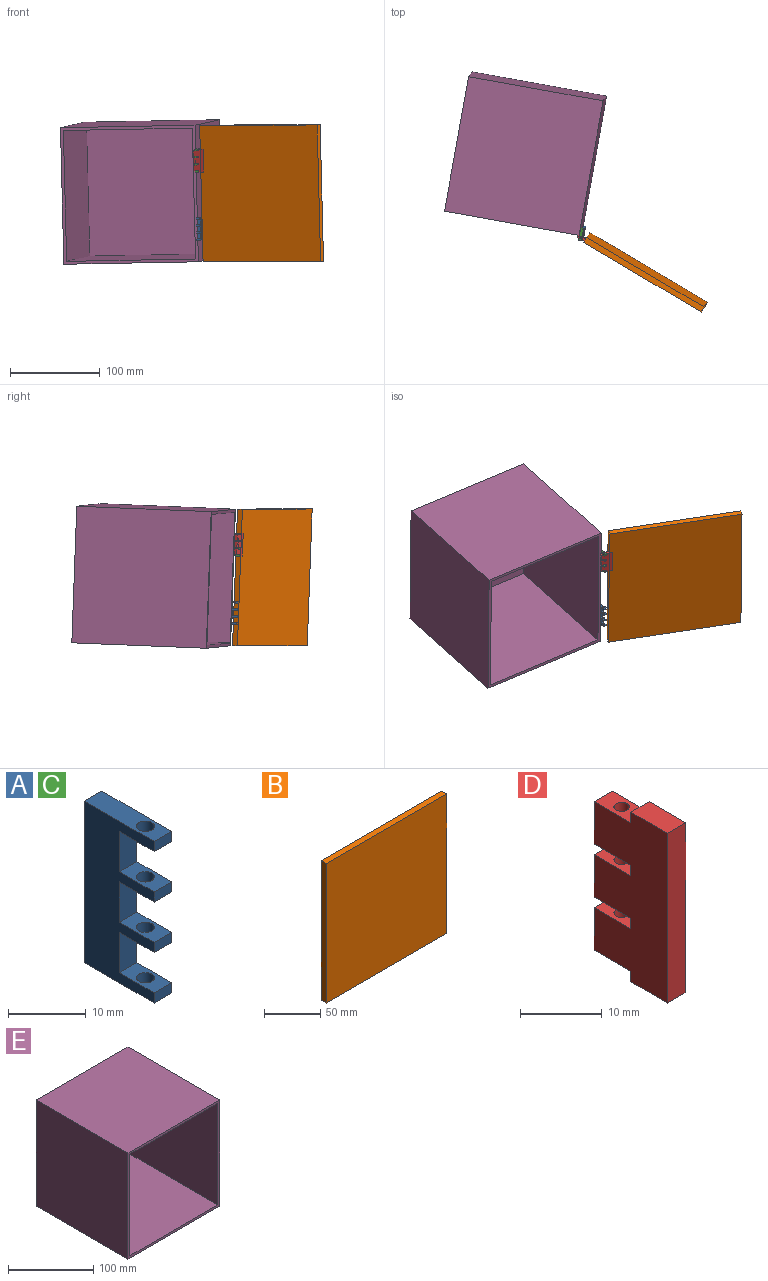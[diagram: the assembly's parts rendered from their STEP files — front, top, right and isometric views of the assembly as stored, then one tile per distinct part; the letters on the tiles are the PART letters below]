
ASSEMBLY  parts=5 mates=8
PART A: 22 faces, bbox 3.2x12.7x25.4 mm
  f0: plane 12.7x3.18mm, normal (0,0,1), area 36.1mm2, adj f1,f15,f16,f17,f21
  f1: plane 3.18x1.59mm, normal (0,-1,0), area 5mm2, adj f0,f2,f16,f17
  f2: plane 6.35x3.18mm, normal (0,0,-1), area 16mm2, adj f1,f3,f16,f17,f21
  f3: plane 6.35x3.18mm, normal (0,-1,0), area 20.2mm2, adj f2,f4,f16,f17
  f4: plane 6.35x3.18mm, normal (0,0,1), area 16mm2, adj f3,f5,f16,f17,f20
  f5: plane 3.18x1.59mm, normal (0,-1,0), area 5mm2, adj f4,f6,f16,f17
  f6: plane 6.35x3.18mm, normal (0,0,-1), area 16mm2, adj f5,f7,f16,f17,f20
  f7: plane 6.35x3.18mm, normal (0,-1,0), area 20.2mm2, adj f6,f8,f16,f17
  f8: plane 6.35x3.18mm, normal (0,0,1), area 16mm2, adj f7,f9,f16,f17,f19
  f9: plane 3.18x1.59mm, normal (0,-1,0), area 5mm2, adj f8,f10,f16,f17
  f10: plane 6.35x3.18mm, normal (0,0,-1), area 16mm2, adj f9,f11,f16,f17,f19
  f11: plane 6.35x3.18mm, normal (0,-1,0), area 20.2mm2, adj f10,f12,f16,f17
  f12: plane 6.35x3.18mm, normal (0,0,1), area 16mm2, adj f11,f13,f16,f17,f18
  f13: plane 3.18x1.59mm, normal (0,-1,0), area 5mm2, adj f12,f14,f16,f17
  f14: plane 12.7x3.18mm, normal (0,0,-1), area 36.1mm2, adj f13,f15,f16,f17,f18
  f15: plane 25.4x3.18mm, normal (0,1,0), area 80.6mm2, adj f0,f14,f16,f17
  f16: plane 25.4x12.7mm, normal (1,0,0), area 201.6mm2, adj f0,f1,f2,f3,f4,f5,f6,f7
  f17: plane 25.4x12.7mm, normal (-1,0,0), area 201.6mm2, adj f0,f1,f2,f3,f4,f5,f6,f7
  f18: cylinder r=1.15mm len=2.31mm, axis (0,0,1), area 11.5mm2, adj f12,f14
  f19: cylinder r=1.15mm len=2.31mm, axis (0,0,1), area 11.5mm2, adj f8,f10
  f20: cylinder r=1.15mm len=2.31mm, axis (0,0,1), area 11.5mm2, adj f4,f6
  f21: cylinder r=1.15mm len=2.31mm, axis (0,0,1), area 11.5mm2, adj f0,f2
PART B: 6 faces, bbox 152.4x6.4x152.4 mm
  f0: plane 152.4x6.35mm, normal (0,0,1), area 967.7mm2, adj f1,f3,f4,f5
  f1: plane 152.4x6.35mm, normal (-1,0,0), area 967.7mm2, adj f0,f2,f4,f5
  f2: plane 152.4x6.35mm, normal (0,0,-1), area 967.7mm2, adj f1,f3,f4,f5
  f3: plane 152.4x6.35mm, normal (1,0,0), area 967.7mm2, adj f0,f2,f4,f5
  f4: plane 152.4x152.4mm, normal (0,-1,0), area 23225.8mm2, adj f0,f1,f2,f3
  f5: plane 152.4x152.4mm, normal (0,1,0), area 23225.8mm2, adj f0,f1,f2,f3
PART C: same geometry as A
PART D: 21 faces, bbox 3.2x12.7x25.4 mm
  f0: plane 3.18x1.59mm, normal (0,1,0), area 5mm2, adj f1,f15,f16,f17
  f1: plane 6.35x3.18mm, normal (0,0,-1), area 17.4mm2, adj f0,f2,f16,f17,f20
  f2: plane 6.35x3.18mm, normal (0,1,0), area 20.2mm2, adj f1,f3,f16,f17
  f3: plane 6.35x3.18mm, normal (0,0,1), area 17.4mm2, adj f2,f4,f16,f17,f20
  f4: plane 3.18x1.59mm, normal (0,1,0), area 5mm2, adj f3,f5,f16,f17
  f5: plane 6.35x3.18mm, normal (0,0,1), area 20.2mm2, adj f4,f6,f16,f17
  f6: plane 25.4x3.18mm, normal (0,-1,0), area 80.6mm2, adj f5,f7,f16,f17
  f7: plane 6.35x3.18mm, normal (0,0,-1), area 20.2mm2, adj f6,f8,f16,f17
  f8: plane 3.18x1.59mm, normal (0,1,0), area 5mm2, adj f7,f9,f16,f17
  f9: plane 6.35x3.18mm, normal (0,0,-1), area 17.4mm2, adj f8,f10,f16,f17,f19
  f10: plane 6.35x3.18mm, normal (0,1,0), area 20.2mm2, adj f9,f11,f16,f17
  f11: plane 6.35x3.18mm, normal (0,0,1), area 17.4mm2, adj f10,f12,f16,f17,f19
  f12: plane 3.18x1.59mm, normal (0,1,0), area 5mm2, adj f11,f13,f16,f17
  f13: plane 6.35x3.18mm, normal (0,0,-1), area 17.4mm2, adj f12,f14,f16,f17,f18
  f14: plane 6.35x3.18mm, normal (0,1,0), area 20.2mm2, adj f13,f15,f16,f17
  f15: plane 6.35x3.18mm, normal (0,0,1), area 17.4mm2, adj f0,f14,f16,f17,f18
  f16: plane 25.4x12.7mm, normal (1,0,0), area 282.3mm2, adj f0,f1,f2,f3,f4,f5,f6,f7
  f17: plane 25.4x12.7mm, normal (-1,0,0), area 282.3mm2, adj f0,f1,f2,f3,f4,f5,f6,f7
  f18: cylinder r=0.94mm len=6.35mm, axis (0,0,1), area 37.4mm2, adj f13,f15
  f19: cylinder r=0.94mm len=6.35mm, axis (0,0,1), area 37.4mm2, adj f9,f11
  f20: cylinder r=0.94mm len=6.35mm, axis (0,0,1), area 37.4mm2, adj f1,f3
PART E: 11 faces, bbox 152.4x152.4x152.4 mm
  f0: plane 152.4x152.4mm, normal (0,-1,0), area 1895.2mm2, adj f1,f3,f4,f5,f6,f7,f8,f9
  f1: plane 152.4x152.4mm, normal (1,0,0), area 23225.8mm2, adj f0,f2,f4,f5
  f2: plane 152.4x152.4mm, normal (0,1,0), area 23225.8mm2, adj f1,f3,f4,f5
  f3: plane 152.4x152.4mm, normal (-1,0,0), area 23225.8mm2, adj f0,f2,f4,f5
  f4: plane 152.4x152.4mm, normal (0,0,1), area 23225.8mm2, adj f0,f1,f2,f3
  f5: plane 152.4x152.4mm, normal (0,0,-1), area 23225.8mm2, adj f0,f1,f2,f3
  f6: plane 146.05x146.05mm, normal (0,0,1), area 21330.6mm2, adj f0,f7,f9,f10
  f7: plane 146.05x146.05mm, normal (-1,0,0), area 21330.6mm2, adj f0,f6,f8,f10
  f8: plane 146.05x146.05mm, normal (0,0,-1), area 21330.6mm2, adj f0,f7,f9,f10
  f9: plane 146.05x146.05mm, normal (1,0,0), area 21330.6mm2, adj f0,f6,f8,f10
  f10: plane 146.05x146.05mm, normal (0,-1,0), area 21330.6mm2, adj f6,f7,f8,f9
PLACE A rot(axis=(0.21,-0.12,-0.97),10.5deg) t=(-404.95,404.01,151.01)mm
PLACE B rot(axis=(-0.01,-0.02,1),149.3deg) t=(-270.15,320.99,254.38)mm
PLACE C rot(axis=(0.21,-0.12,-0.97),10.5deg) t=(-406.84,401.25,227.13)mm
PLACE D rot(axis=(0.02,-0.04,1),59.4deg) t=(-402.82,401.77,214.54)mm
PLACE E rot(axis=(0.21,-0.12,-0.97),10.5deg) t=(-464.13,500.5,103.52)mm
MATE planar C.f17 <-> E.f1  axis (-0.98,0.18,-0.02) through (-405.07,409.83,214.78)mm
MATE planar B.f0 <-> E.f4  axis (-0.02,-0.04,1) through (-401.19,398.79,253.94)mm
MATE planar C.f3 <-> E.f0  axis (-0.18,-0.98,-0.04) through (-404.04,407.38,222.66)mm
MATE planar D.f17 <-> B.f5  axis (-0.51,-0.86,-0.04) through (-402.09,401.33,214.54)mm
MATE planar C.f3 <-> E.f0  axis (-0.18,-0.98,-0.04) through (-404.04,407.38,222.66)mm
MATE revolute D.f18 <-> C.f18  axis (-0.02,-0.04,1) through (-404.68,404.15,225.7)mm
MATE planar D.f16 <-> B.f5  axis (0.51,0.86,0.04) through (-400.47,404.06,214.68)mm
MATE parallel E.f4 <-> B.f0  axis (-0.02,-0.04,1) through (-406.39,406.53,254.09)mm
